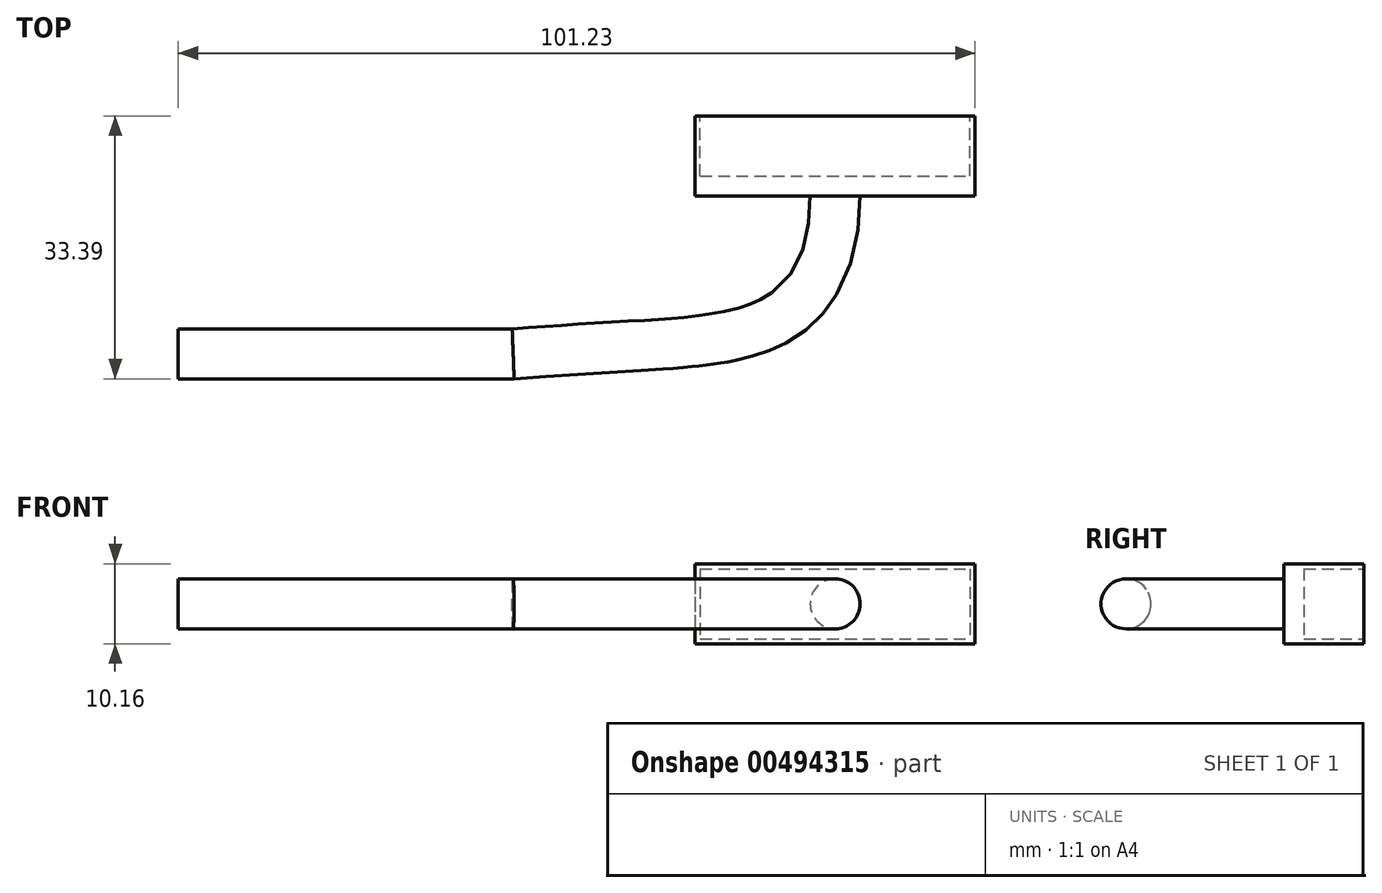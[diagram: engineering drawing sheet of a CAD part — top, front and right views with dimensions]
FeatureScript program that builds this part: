
annotation { "Feature Type Name" : "Feature", "Feature Type Description" : "" }
export const myFeature = defineFeature(function(context is Context, id is Id, definition is map)
    precondition{}
    {
        {
            var Q0;
            Q0=qCreatedBy(makeId("Front.planeOp"),FACE);
            var sketch = newSketch(context, id + "F0", { "sketchPlane" : qUnion([Q0])});
            skLineSegment(sketch, "E0.bottom", {"start": v(17.78, 5.08) * mm, "end": v(-17.78, 5.08) * mm});
            skLineSegment(sketch, "E0.top", {"start": v(17.78, -5.08) * mm, "end": v(-17.78, -5.08) * mm});
            skLineSegment(sketch, "E0.left", {"start": v(17.78, 5.08) * mm, "end": v(17.78, -5.08) * mm});
            skLineSegment(sketch, "E0.right", {"start": v(-17.78, 5.08) * mm, "end": v(-17.78, -5.08) * mm});
            skPoint(sketch, "E0.middle", {"position": v(0, 0) * mm});
            skSolve(sketch);
        }
        {
            var Q0;
            Q0=qSketchRegion(id+"F0",true);
            extrude(context, id + "F1", {"entities" : qUnion([Q0]), "oppositeDirection" : true, "depth" : 10.16 * mm});
        }
        {
            var Q0;
            Q0=makeQuery(id+"F1.opExtrude","CAP_FACE",FACE,{"disambiguationData":[OSD([sQuery(id+"F0.wireOp",EDGE,"E0.bottom"),sQuery(id+"F0.wireOp",EDGE,"E0.top"),sQuery(id+"F0.wireOp",EDGE,"E0.left"),sQuery(id+"F0.wireOp",EDGE,"E0.right")])],"isStart":false});
            var sketch = newSketch(context, id + "F2", { "sketchPlane" : qUnion([Q0])});
            skLineSegment(sketch, "E1.bottom", {"start": v(17.15, 4.45) * mm, "end": v(-17.15, 4.45) * mm});
            skLineSegment(sketch, "E1.top", {"start": v(17.15, -4.45) * mm, "end": v(-17.15, -4.45) * mm});
            skLineSegment(sketch, "E1.left", {"start": v(17.15, 4.45) * mm, "end": v(17.15, -4.45) * mm});
            skLineSegment(sketch, "E1.right", {"start": v(-17.15, 4.45) * mm, "end": v(-17.15, -4.45) * mm});
            skPoint(sketch, "E1.middle", {"position": v(0, 0) * mm});
            skSolve(sketch);
        }
        {
            var Q0;
            Q0=qSketchRegion(id+"F2",true);
            extrude(context, id + "F3", {"entities" : qUnion([Q0]), "operationType" : NewBodyOperationType.REMOVE, "oppositeDirection" : true, "depth" : 7.62 * mm});
        }
        {
            var Q0;
            Q0=qCreatedBy(makeId("Top.planeOp"),FACE);
            var sketch = newSketch(context, id + "F4", { "sketchPlane" : qUnion([Q0])});
            skFitSpline(sketch, "E2", {"points": [v(0, 0) * mm, v(-16.2, -18.24) * mm, v(-40.9, -20.06) * mm], "startDerivative": vector(0, -93.27) * mm, "endDerivative": vector(-99.99, -7.63) * mm});
            skLineSegment(sketch, "E3", {"start": v(-40.9, -20.06) * mm, "end": v(-83.45, -20.06) * mm});
            skSolve(sketch);
        }
        {
            var Q0;
            Q0=makeQuery(id+"F1.opExtrude","CAP_FACE",FACE,{"disambiguationData":[OSD([sQuery(id+"F0.wireOp",EDGE,"E0.bottom"),sQuery(id+"F0.wireOp",EDGE,"E0.top"),sQuery(id+"F0.wireOp",EDGE,"E0.left"),sQuery(id+"F0.wireOp",EDGE,"E0.right")])],"isStart":true});
            var sketch = newSketch(context, id + "F5", { "sketchPlane" : qUnion([Q0])});
            skEllipse(sketch, "E4", {"center": v(0, 0) * mm, "majorRadius": 3.18 * mm, "minorRadius": 3.18 * mm, "majorAxis": v(1, 0)});
            skSolve(sketch);
        }
        {
            var Q0;
            Q0=makeQuery(id+"F5.imprint","IMPRINT",FACE,{"disambiguationData":[TD([[makeQuery(id+"F5.imprint","IMPRINT",EDGE,{"derivedFrom":sQuery(id+"F5.wireOp",EDGE,"E4")}),1.0]])]});
            var Q1;
            Q1=sQuery(id+"F4.wireOp",EDGE,"E2");
            var Q2;
            Q2=sQuery(id+"F4.wireOp",EDGE,"E3");
            sweep(context, id + "F6", {"operationType" : NewBodyOperationType.ADD, "profiles" : qUnion([Q0]), "path" : qUnion([Q1, Q2])});
        }
    });
